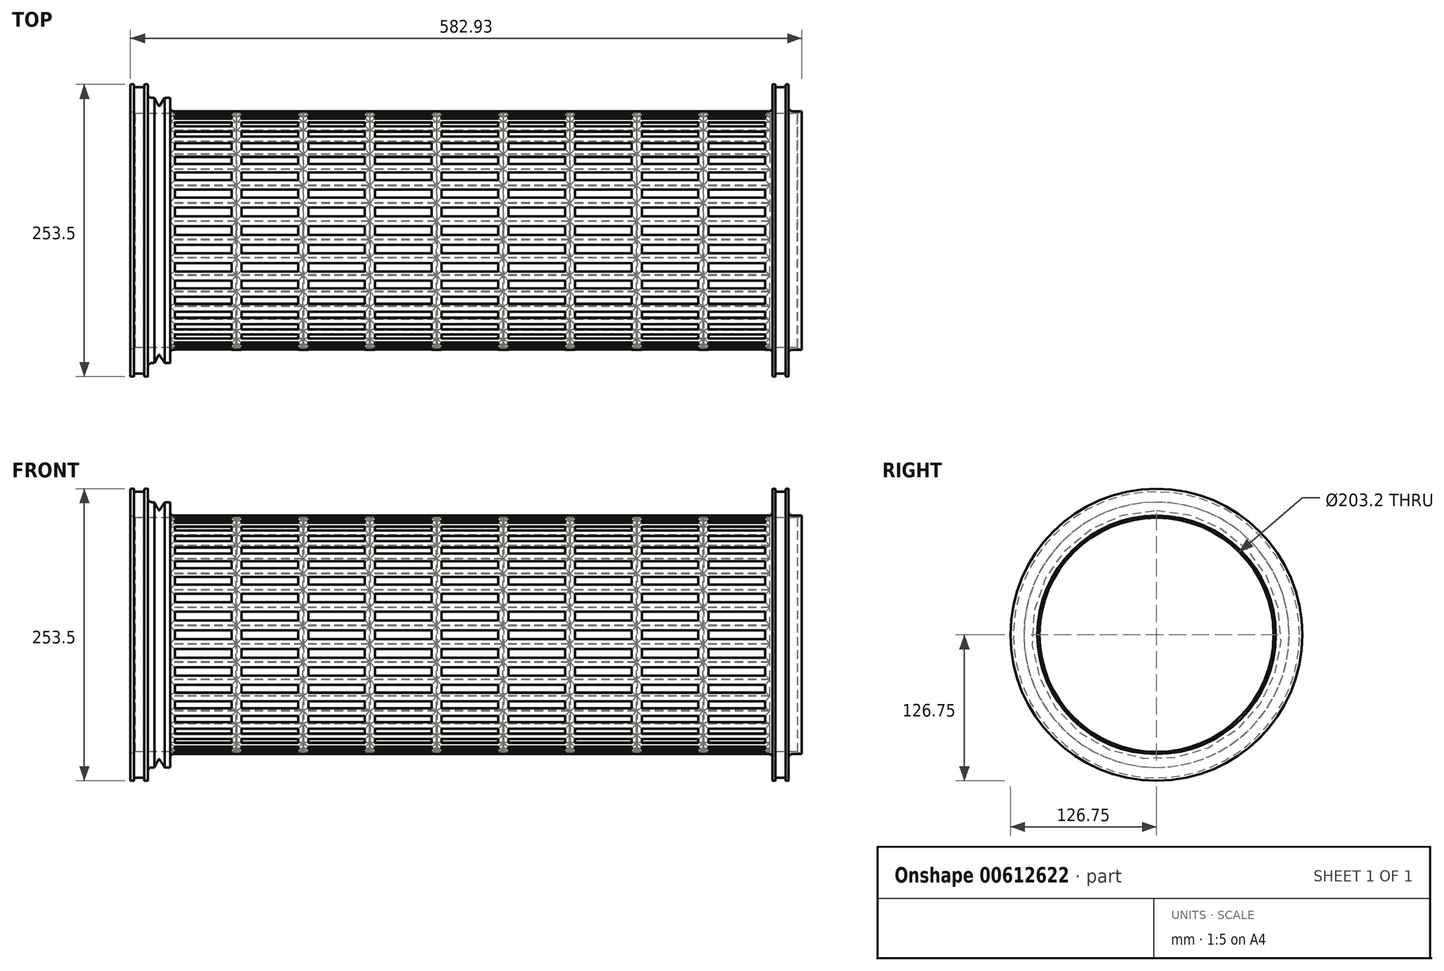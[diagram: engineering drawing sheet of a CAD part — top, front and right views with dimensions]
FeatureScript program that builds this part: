
annotation { "Feature Type Name" : "Feature", "Feature Type Description" : "" }
export const myFeature = defineFeature(function(context is Context, id is Id, definition is map)
    precondition{}
    {
        {
            var Q0;
            Q0=qCreatedBy(makeId("Top.planeOp"),FACE);
            var sketch = newSketch(context, id + "F0", { "sketchPlane" : qUnion([Q0])});
            skLineSegment(sketch, "E0", {"start": v(-334.6, 103.5) * mm, "end": v(-334.6, 126.75) * mm});
            skLineSegment(sketch, "E1", {"start": v(-334.6, 126.75) * mm, "end": v(-331.43, 126.75) * mm});
            skLineSegment(sketch, "E2", {"start": v(-319.37, 126.75) * mm, "end": v(-319.37, 103.5) * mm});
            skLineSegment(sketch, "E3", {"start": v(-319.37, 103.5) * mm, "end": v(222.92, 103.5) * mm});
            skLineSegment(sketch, "E4", {"start": v(222.92, 103.5) * mm, "end": v(222.92, 126.75) * mm});
            skLineSegment(sketch, "E5", {"start": v(236.9, 126.75) * mm, "end": v(236.9, 103.5) * mm});
            skLineSegment(sketch, "E6", {"start": v(236.9, 103.5) * mm, "end": v(248.32, 103.5) * mm});
            skLineSegment(sketch, "E7", {"start": v(-334.6, 101.6) * mm, "end": v(248.32, 101.6) * mm});
            skLineSegment(sketch, "E8", {"start": v(248.32, 101.6) * mm, "end": v(248.32, 103.5) * mm});
            skLineSegment(sketch, "E9", {"start": v(-331.43, 126.75) * mm, "end": v(-331.43, 124.2) * mm});
            skLineSegment(sketch, "E10", {"start": v(-322.54, 124.2) * mm, "end": v(-322.54, 126.75) * mm});
            skLineSegment(sketch, "E11.trimOffspring", {"start": v(-322.54, 126.75) * mm, "end": v(-319.37, 126.75) * mm});
            skLineSegment(sketch, "E12", {"start": v(225.46, 126.75) * mm, "end": v(225.46, 124.2) * mm});
            skLineSegment(sketch, "E13", {"start": v(-300.16, 103.5) * mm, "end": v(-300.16, 115.13) * mm});
            skPoint(sketch, "E13.endSnap0", {"position": v(-319.37, 115.13) * mm});
            skLineSegment(sketch, "E14", {"start": v(-300.16, 115.13) * mm, "end": v(-304.87, 115.13) * mm});
            skLineSegment(sketch, "E15", {"start": v(-313.74, 115.13) * mm, "end": v(-309.76, 107.51) * mm});
            skPoint(sketch, "E15.endSnap0", {"position": v(-309.76, 115.13) * mm});
            skLineSegment(sketch, "E16", {"start": v(-309.76, 107.51) * mm, "end": v(-304.87, 115.13) * mm});
            skLineSegment(sketch, "E17.trimOffspring", {"start": v(-313.74, 115.13) * mm, "end": v(-319.37, 115.13) * mm});
            skLineSegment(sketch, "E18", {"start": v(-334.6, 103.5) * mm, "end": v(-334.6, 101.6) * mm});
            skPoint(sketch, "E19.end.orphan", {"position": v(-353.66, 101.6) * mm});
            skLineSegment(sketch, "E20", {"start": v(222.92, 126.75) * mm, "end": v(225.46, 126.75) * mm});
            skPoint(sketch, "E20.startSnap0", {"position": v(225.46, 126.75) * mm});
            skPoint(sketch, "E21.start.orphan", {"position": v(222.92, 126.75) * mm});
            skPoint(sketch, "E22.orphan", {"position": v(225.46, 129.3) * mm});
            skPoint(sketch, "E23.trimOffspring.start.orphan", {"position": v(233.08, 126.75) * mm});
            skPoint(sketch, "E24.end.orphan", {"position": v(233.08, 124.2) * mm});
            skLineSegment(sketch, "E25", {"start": v(225.46, 124.2) * mm, "end": v(234.35, 124.2) * mm});
            skLineSegment(sketch, "E26", {"start": v(234.35, 124.2) * mm, "end": v(234.35, 126.11) * mm});
            skPoint(sketch, "E26.endSnap0", {"position": v(234.99, 126.11) * mm});
            skPoint(sketch, "E27.orphan", {"position": v(233.08, 125.48) * mm});
            skLineSegment(sketch, "E28", {"start": v(-331.43, 124.2) * mm, "end": v(-322.54, 124.2) * mm});
            skLineSegment(sketch, "E29", {"start": v(234.35, 126.11) * mm, "end": v(234.35, 126.75) * mm});
            skLineSegment(sketch, "E30", {"start": v(234.35, 126.75) * mm, "end": v(236.9, 126.75) * mm});
            skSolve(sketch);
        }
        {
            var Q0;
            Q0=qCreatedBy(makeId("Top.planeOp"),FACE);
            var sketch = newSketch(context, id + "F1", { "sketchPlane" : qUnion([Q0])});
            skLineSegment(sketch, "E31", {"start": v(-76.35, 0) * mm, "end": v(75.96, 0) * mm});
            skSolve(sketch);
        }
        {
            var Q0;
            Q0=makeQuery(id+"F0.imprint","IMPRINT",FACE,{"disambiguationData":[TD([[makeQuery(id+"F0.imprint","IMPRINT",EDGE,{"derivedFrom":sQuery(id+"F0.wireOp",EDGE,"E0")}),-1.0]])]});
            var Q1;
            {var subQ0=sQuery(id+"F0.wireOp",EDGE,"E13");Q1=makeQuery(id+"F0.imprint","IMPRINT",FACE,{"disambiguationData":[TD([[makeQuery(id+"F0.imprint","IMPRINT",EDGE,{"derivedFrom":subQ0}),1.0]])]});}
            var Q2;
            Q2 = qSketchRegion(id + "F3", true);
            var Q3;
            Q3=sQuery(id+"F1.wireOp",EDGE,"E31");
            revolve(context, id + "F2", {"entities" : qUnion([Q0, Q1, Q2]), "axis" : qUnion([Q3]), "revolveType" : RevolveType.FULL, "surfaceOperationType" : NewSurfaceOperationType.NEW});
        }
        {
            var Q0;
            Q0=qCreatedBy(makeId("Top.planeOp"),FACE);
            var sketch = newSketch(context, id + "F3", { "sketchPlane" : qUnion([Q0])});
            skPoint(sketch, "E32.middle", {"position": v(-205.28, 0) * mm});
            skPoint(sketch, "E33.middle", {"position": v(0, 0) * mm});
            skPoint(sketch, "E34.middle", {"position": v(166.22, 0) * mm});
            skLineSegment(sketch, "E35", {"start": v(-296.04, -3.81) * mm, "end": v(-296.04, 3.81) * mm});
            skPoint(sketch, "E36.orphan", {"position": v(-306.88, -3.81) * mm});
            skPoint(sketch, "E37.orphan", {"position": v(-306.88, 3.81) * mm});
            skPoint(sketch, "E34.left.start.orphan", {"position": v(229.72, -3.81) * mm});
            skPoint(sketch, "E38.orphan", {"position": v(229.72, 3.8) * mm});
            skLineSegment(sketch, "E39", {"start": v(-246.86, 3.81) * mm, "end": v(-246.86, -3.81) * mm});
            skLineSegment(sketch, "E40.trimOffspring", {"start": v(-246.86, 3.81) * mm, "end": v(-296.04, 3.81) * mm});
            skLineSegment(sketch, "E41.trimOffspring", {"start": v(-246.86, -3.81) * mm, "end": v(-296.04, -3.81) * mm});
            skPoint(sketch, "E42.end.orphan", {"position": v(-171.63, 3.81) * mm});
            skPoint(sketch, "E42.start.orphan", {"position": v(-171.63, -3.81) * mm});
            skPoint(sketch, "E43.end.orphan", {"position": v(-239.58, -3.81) * mm});
            skPoint(sketch, "E43.start.orphan", {"position": v(-239.58, 3.81) * mm});
            skPoint(sketch, "E32.left.end.orphan", {"position": v(-103.68, 3.81) * mm});
            skPoint(sketch, "E32.left.start.orphan", {"position": v(-103.68, -3.8) * mm});
            skPoint(sketch, "E33.bottom.end.orphan", {"position": v(-93.22, 3.98) * mm});
            skPoint(sketch, "E33.top.end.orphan", {"position": v(-93.22, -3.98) * mm});
            skPoint(sketch, "E33.left.end.orphan", {"position": v(93.22, -3.98) * mm});
            skPoint(sketch, "E33.left.start.orphan", {"position": v(93.22, 3.98) * mm});
            skPoint(sketch, "E34.bottom.end.orphan", {"position": v(102.72, -3.81) * mm});
            skPoint(sketch, "E34.top.end.orphan", {"position": v(102.72, 3.8) * mm});
            skLineSegment(sketch, "E44.1.0.0", {"start": v(-238.12, -3.81) * mm, "end": v(-238.12, 3.81) * mm});
            skLineSegment(sketch, "E44.1.0.1", {"start": v(-188.95, -3.81) * mm, "end": v(-238.12, -3.81) * mm});
            skLineSegment(sketch, "E44.1.0.2", {"start": v(-188.95, 3.81) * mm, "end": v(-188.95, -3.81) * mm});
            skLineSegment(sketch, "E44.1.0.3", {"start": v(-188.95, 3.81) * mm, "end": v(-238.12, 3.81) * mm});
            skLineSegment(sketch, "E44.2.0.0", {"start": v(-180.21, -3.81) * mm, "end": v(-180.21, 3.81) * mm});
            skLineSegment(sketch, "E44.2.0.1", {"start": v(-131.04, -3.81) * mm, "end": v(-180.21, -3.81) * mm});
            skLineSegment(sketch, "E44.2.0.2", {"start": v(-131.04, 3.81) * mm, "end": v(-131.04, -3.81) * mm});
            skLineSegment(sketch, "E44.2.0.3", {"start": v(-131.04, 3.81) * mm, "end": v(-180.21, 3.81) * mm});
            skLineSegment(sketch, "E44.3.0.0", {"start": v(-122.3, -3.81) * mm, "end": v(-122.3, 3.81) * mm});
            skLineSegment(sketch, "E44.3.0.1", {"start": v(-73.13, -3.81) * mm, "end": v(-122.3, -3.81) * mm});
            skLineSegment(sketch, "E44.3.0.2", {"start": v(-73.13, 3.81) * mm, "end": v(-73.13, -3.81) * mm});
            skLineSegment(sketch, "E44.3.0.3", {"start": v(-73.13, 3.81) * mm, "end": v(-122.3, 3.81) * mm});
            skLineSegment(sketch, "E44.4.0.0", {"start": v(-64.39, -3.81) * mm, "end": v(-64.39, 3.81) * mm});
            skLineSegment(sketch, "E44.4.0.1", {"start": v(-15.22, -3.81) * mm, "end": v(-64.39, -3.81) * mm});
            skLineSegment(sketch, "E44.4.0.2", {"start": v(-15.22, 3.81) * mm, "end": v(-15.22, -3.81) * mm});
            skLineSegment(sketch, "E44.4.0.3", {"start": v(-15.22, 3.81) * mm, "end": v(-64.39, 3.81) * mm});
            skLineSegment(sketch, "E44.5.0.0", {"start": v(-6.48, -3.81) * mm, "end": v(-6.48, 3.81) * mm});
            skLineSegment(sketch, "E44.5.0.1", {"start": v(42.7, -3.81) * mm, "end": v(-6.48, -3.81) * mm});
            skLineSegment(sketch, "E44.5.0.2", {"start": v(42.7, 3.81) * mm, "end": v(42.7, -3.81) * mm});
            skLineSegment(sketch, "E44.5.0.3", {"start": v(42.7, 3.81) * mm, "end": v(-6.48, 3.81) * mm});
            skLineSegment(sketch, "E44.6.0.0", {"start": v(51.44, -3.81) * mm, "end": v(51.44, 3.81) * mm});
            skLineSegment(sketch, "E44.6.0.1", {"start": v(100.6, -3.81) * mm, "end": v(51.44, -3.81) * mm});
            skLineSegment(sketch, "E44.6.0.2", {"start": v(100.6, 3.81) * mm, "end": v(100.6, -3.81) * mm});
            skLineSegment(sketch, "E44.6.0.3", {"start": v(100.6, 3.81) * mm, "end": v(51.44, 3.81) * mm});
            skLineSegment(sketch, "E44.7.0.0", {"start": v(109.35, -3.81) * mm, "end": v(109.35, 3.81) * mm});
            skLineSegment(sketch, "E44.7.0.1", {"start": v(158.52, -3.81) * mm, "end": v(109.35, -3.81) * mm});
            skLineSegment(sketch, "E44.7.0.2", {"start": v(158.52, 3.81) * mm, "end": v(158.52, -3.81) * mm});
            skLineSegment(sketch, "E44.7.0.3", {"start": v(158.52, 3.81) * mm, "end": v(109.35, 3.81) * mm});
            skLineSegment(sketch, "E44.8.0.0", {"start": v(167.26, -3.81) * mm, "end": v(167.26, 3.81) * mm});
            skLineSegment(sketch, "E44.8.0.1", {"start": v(216.43, -3.81) * mm, "end": v(167.26, -3.81) * mm});
            skLineSegment(sketch, "E44.8.0.2", {"start": v(216.43, 3.81) * mm, "end": v(216.43, -3.81) * mm});
            skLineSegment(sketch, "E44.8.0.3", {"start": v(216.43, 3.81) * mm, "end": v(167.26, 3.81) * mm});
            skLineSegment(sketch, "E44.direction1", {"start": v(-296.04, -3.81) * mm, "end": v(-238.12, -3.81) * mm, "construction": true});
            skSolve(sketch);
        }
        {
            var Q0;
            Q0=qSketchRegion(id+"F3",true);
            extrude(context, id + "F4", {"entities" : qUnion([Q0]), "depth" : 114.3 * mm, "offsetDistance" : 25.4 * mm});
        }
        {
            var Q0;
            Q0=makeQuery(id+"F4.opExtrude","SWEPT_BODY",BODY,{"disambiguationData":[OSD([sQuery(id+"F3.wireOp",EDGE,"E44.8.0.0"),sQuery(id+"F3.wireOp",EDGE,"E44.8.0.1"),sQuery(id+"F3.wireOp",EDGE,"E44.8.0.2"),sQuery(id+"F3.wireOp",EDGE,"E44.8.0.3")])]});
            var Q1;
            Q1=makeQuery(id+"F4.opExtrude","SWEPT_BODY",BODY,{"disambiguationData":[OSD([sQuery(id+"F3.wireOp",EDGE,"E44.7.0.0"),sQuery(id+"F3.wireOp",EDGE,"E44.7.0.1"),sQuery(id+"F3.wireOp",EDGE,"E44.7.0.2"),sQuery(id+"F3.wireOp",EDGE,"E44.7.0.3")])]});
            var Q2;
            Q2=makeQuery(id+"F4.opExtrude","SWEPT_BODY",BODY,{"disambiguationData":[OSD([sQuery(id+"F3.wireOp",EDGE,"E44.6.0.0"),sQuery(id+"F3.wireOp",EDGE,"E44.6.0.1"),sQuery(id+"F3.wireOp",EDGE,"E44.6.0.2"),sQuery(id+"F3.wireOp",EDGE,"E44.6.0.3")])]});
            var Q3;
            Q3=makeQuery(id+"F4.opExtrude","SWEPT_BODY",BODY,{"disambiguationData":[OSD([sQuery(id+"F3.wireOp",EDGE,"E44.5.0.0"),sQuery(id+"F3.wireOp",EDGE,"E44.5.0.1"),sQuery(id+"F3.wireOp",EDGE,"E44.5.0.2"),sQuery(id+"F3.wireOp",EDGE,"E44.5.0.3")])]});
            var Q4;
            Q4=makeQuery(id+"F4.opExtrude","SWEPT_BODY",BODY,{"disambiguationData":[OSD([sQuery(id+"F3.wireOp",EDGE,"E44.4.0.0"),sQuery(id+"F3.wireOp",EDGE,"E44.4.0.1"),sQuery(id+"F3.wireOp",EDGE,"E44.4.0.2"),sQuery(id+"F3.wireOp",EDGE,"E44.4.0.3")])]});
            var Q5;
            Q5=makeQuery(id+"F4.opExtrude","SWEPT_BODY",BODY,{"disambiguationData":[OSD([sQuery(id+"F3.wireOp",EDGE,"E44.3.0.0"),sQuery(id+"F3.wireOp",EDGE,"E44.3.0.1"),sQuery(id+"F3.wireOp",EDGE,"E44.3.0.2"),sQuery(id+"F3.wireOp",EDGE,"E44.3.0.3")])]});
            var Q6;
            Q6=makeQuery(id+"F4.opExtrude","SWEPT_BODY",BODY,{"disambiguationData":[OSD([sQuery(id+"F3.wireOp",EDGE,"E44.2.0.0"),sQuery(id+"F3.wireOp",EDGE,"E44.2.0.1"),sQuery(id+"F3.wireOp",EDGE,"E44.2.0.2"),sQuery(id+"F3.wireOp",EDGE,"E44.2.0.3")])]});
            var Q7;
            Q7=makeQuery(id+"F4.opExtrude","SWEPT_BODY",BODY,{"disambiguationData":[OSD([sQuery(id+"F3.wireOp",EDGE,"E44.1.0.0"),sQuery(id+"F3.wireOp",EDGE,"E44.1.0.1"),sQuery(id+"F3.wireOp",EDGE,"E44.1.0.2"),sQuery(id+"F3.wireOp",EDGE,"E44.1.0.3")])]});
            var Q8;
            Q8=makeQuery(id+"F4.opExtrude","SWEPT_BODY",BODY,{"disambiguationData":[OSD([sQuery(id+"F3.wireOp",EDGE,"E35"),sQuery(id+"F3.wireOp",EDGE,"E39"),sQuery(id+"F3.wireOp",EDGE,"E40.trimOffspring"),sQuery(id+"F3.wireOp",EDGE,"E41.trimOffspring")])]});
            var Q9;
            Q9=makeQuery(id+"F2.opRevolve","SWEPT_FACE",FACE,{"disambiguationData":[OSD([sQuery(id+"F0.wireOp",EDGE,"E7")])]});
            circularPattern(context, id + "F5", {"operationType" : NewBodyOperationType.REMOVE, "entities" : qUnion([Q0, Q1, Q2, Q3, Q4, Q5, Q6, Q7, Q8]), "axis" : qUnion([Q9]), "angle" : 360 * degree, "instanceCount" : 40, "equalSpace" : true});
        }
        {
            var Q0;
            Q0=makeQuery(id+"F2.opRevolve","SWEPT_FACE",FACE,{"disambiguationData":[OSD([sQuery(id+"F0.wireOp",EDGE,"E7")])]});
            chamfer(context, id + "F6", {"entities" : qUnion([Q0]), "chamferType" : ChamferType.TWO_OFFSETS, "width1" : 4.06 * mm, "oppositeDirection" : false, "width2" : 1.9 * mm});
        }
        {
            var Q0;
            Q0=makeQuery(id+"F2.opRevolve","SWEPT_EDGE",EDGE,{"disambiguationData":[OSD([sQuery(id+"F0.wireOp",EDGE,"E2"),sQuery(id+"F0.wireOp",EDGE,"E17.trimOffspring")])]});
            var Q1;
            Q1=makeQuery(id+"F2.opRevolve","SWEPT_EDGE",EDGE,{"disambiguationData":[OSD([sQuery(id+"F0.wireOp",EDGE,"E3"),sQuery(id+"F0.wireOp",EDGE,"E13")])]});
            var Q2;
            Q2=makeQuery(id+"F2.opRevolve","SWEPT_EDGE",EDGE,{"disambiguationData":[OSD([sQuery(id+"F0.wireOp",EDGE,"E3"),sQuery(id+"F0.wireOp",EDGE,"E4")])]});
            var Q3;
            Q3=makeQuery(id+"F2.opRevolve","SWEPT_EDGE",EDGE,{"disambiguationData":[OSD([sQuery(id+"F0.wireOp",EDGE,"E5"),sQuery(id+"F0.wireOp",EDGE,"E6")])]});
            fillet(context, id + "F7", {"entities" : qUnion([Q0, Q1, Q2, Q3]), "radius" : 3.17 * mm, "tangentPropagation" : true, "allowEdgeOverflow" : false});
        }
        {
            var Q0;
            Q0=makeQuery(id+"F2.opRevolve","SWEPT_EDGE",EDGE,{"disambiguationData":[OSD([sQuery(id+"F0.wireOp",EDGE,"E10"),sQuery(id+"F0.wireOp",EDGE,"E28")])]});
            var Q1;
            Q1=makeQuery(id+"F2.opRevolve","SWEPT_EDGE",EDGE,{"disambiguationData":[OSD([sQuery(id+"F0.wireOp",EDGE,"E15"),sQuery(id+"F0.wireOp",EDGE,"E16")])]});
            var Q2;
            Q2=makeQuery(id+"F2.opRevolve","SWEPT_EDGE",EDGE,{"disambiguationData":[OSD([sQuery(id+"F0.wireOp",EDGE,"E13"),sQuery(id+"F0.wireOp",EDGE,"E14")])]});
            var Q3;
            Q3=makeQuery(id+"F2.opRevolve","SWEPT_EDGE",EDGE,{"disambiguationData":[OSD([sQuery(id+"F0.wireOp",EDGE,"E25"),sQuery(id+"F0.wireOp",EDGE,"E26")])]});
            var Q4;
            Q4=makeQuery(id+"F2.opRevolve","SWEPT_EDGE",EDGE,{"disambiguationData":[OSD([sQuery(id+"F0.wireOp",EDGE,"E4"),sQuery(id+"F0.wireOp",EDGE,"E20")])]});
            var Q5;
            Q5=makeQuery(id+"F2.opRevolve","SWEPT_EDGE",EDGE,{"disambiguationData":[OSD([sQuery(id+"F0.wireOp",EDGE,"E29"),sQuery(id+"F0.wireOp",EDGE,"E30")])]});
            var Q6;
            Q6=makeQuery(id+"F2.opRevolve","SWEPT_EDGE",EDGE,{"disambiguationData":[OSD([sQuery(id+"F0.wireOp",EDGE,"E5"),sQuery(id+"F0.wireOp",EDGE,"E30")])]});
            var Q7;
            Q7=makeQuery(id+"F2.opRevolve","SWEPT_EDGE",EDGE,{"disambiguationData":[OSD([sQuery(id+"F0.wireOp",EDGE,"E12"),sQuery(id+"F0.wireOp",EDGE,"E20")])]});
            var Q8;
            Q8=makeQuery(id+"F2.opRevolve","SWEPT_EDGE",EDGE,{"disambiguationData":[OSD([sQuery(id+"F0.wireOp",EDGE,"E10"),sQuery(id+"F0.wireOp",EDGE,"E11.trimOffspring")])]});
            var Q9;
            Q9=makeQuery(id+"F2.opRevolve","SWEPT_EDGE",EDGE,{"disambiguationData":[OSD([sQuery(id+"F0.wireOp",EDGE,"E0"),sQuery(id+"F0.wireOp",EDGE,"E1")])]});
            var Q10;
            Q10=makeQuery(id+"F2.opRevolve","SWEPT_EDGE",EDGE,{"disambiguationData":[OSD([sQuery(id+"F0.wireOp",EDGE,"E1"),sQuery(id+"F0.wireOp",EDGE,"E9")])]});
            var Q11;
            Q11=makeQuery(id+"F2.opRevolve","SWEPT_EDGE",EDGE,{"disambiguationData":[OSD([sQuery(id+"F0.wireOp",EDGE,"E2"),sQuery(id+"F0.wireOp",EDGE,"E11.trimOffspring")])]});
            fillet(context, id + "F8", {"entities" : qUnion([Q0, Q1, Q2, Q3, Q4, Q5, Q6, Q7, Q8, Q9, Q10, Q11]), "radius" : 0.5 * mm, "tangentPropagation" : true, "allowEdgeOverflow" : false});
        }
    });
